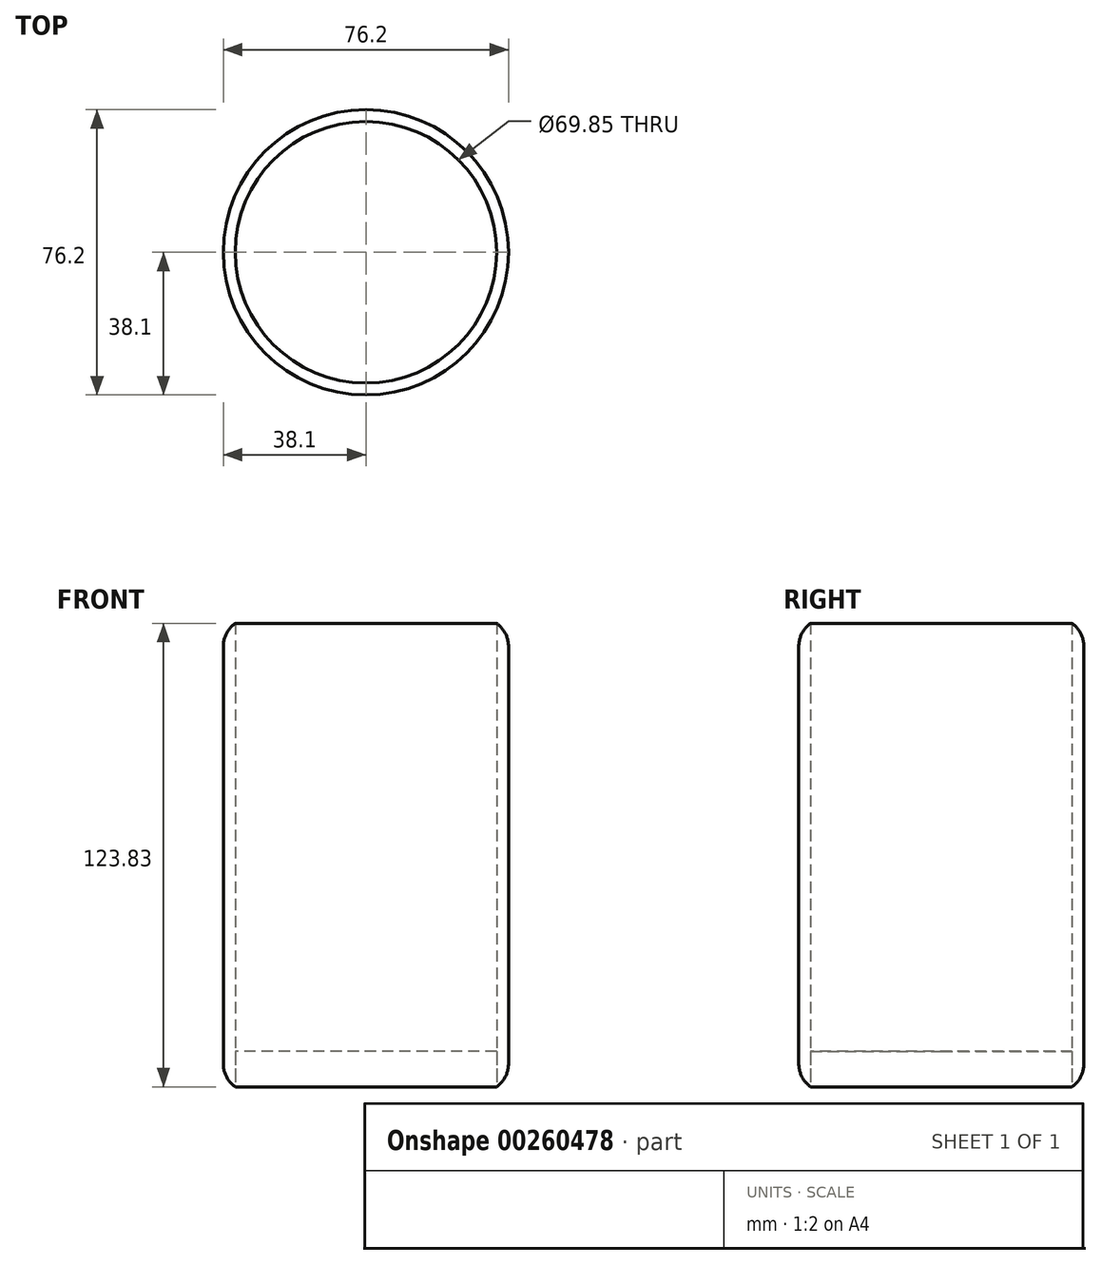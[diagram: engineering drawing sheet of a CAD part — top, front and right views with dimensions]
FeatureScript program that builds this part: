
annotation { "Feature Type Name" : "Feature", "Feature Type Description" : "" }
export const myFeature = defineFeature(function(context is Context, id is Id, definition is map)
    precondition{}
    {
        {
            var Q0;
            Q0=qCreatedBy(makeId("Top.planeOp"),FACE);
            var sketch = newSketch(context, id + "F0", { "sketchPlane" : qUnion([Q0])});
            skCircle(sketch, "E0", {"center": v(0, 0) * mm, "radius": 38.1 * mm});
            skCircle(sketch, "E1", {"center": v(0, 0) * mm, "radius": 34.93 * mm});
            skSolve(sketch);
        }
        {
            var Q0;
            Q0=makeQuery(id+"F0.imprint","IMPRINT",FACE,{"disambiguationData":[TD([[makeQuery(id+"F0.imprint","IMPRINT",EDGE,{"derivedFrom":sQuery(id+"F0.wireOp",EDGE,"E0")}),1.0]])]});
            extrude(context, id + "F1", {"entities" : qUnion([Q0]), "depth" : 123.82 * mm});
        }
        {
            var Q0;
            Q0=makeQuery(id+"F0.imprint","IMPRINT",FACE,{"disambiguationData":[TD([[makeQuery(id+"F0.imprint","IMPRINT",EDGE,{"derivedFrom":sQuery(id+"F0.wireOp",EDGE,"E1")}),1.0]])]});
            extrude(context, id + "F2", {"entities" : qUnion([Q0]), "depth" : 9.52 * mm});
        }
        {
            var Q0;
            Q0=makeQuery(id+"F1.opExtrude","CAP_EDGE",EDGE,{"disambiguationData":[OSD([sQuery(id+"F0.wireOp",EDGE,"E0")])],"isStart":false});
            fillet(context, id + "F3", {"entities" : qUnion([Q0]), "radius" : 7.62 * mm, "tangentPropagation" : true, "allowEdgeOverflow" : false});
        }
        {
            var Q0;
            Q0=makeQuery(id+"F1.opExtrude","CAP_EDGE",EDGE,{"disambiguationData":[OSD([sQuery(id+"F0.wireOp",EDGE,"E0")])],"isStart":true});
            fillet(context, id + "F4", {"entities" : qUnion([Q0]), "radius" : 7.62 * mm, "tangentPropagation" : true, "allowEdgeOverflow" : false});
        }
    });
